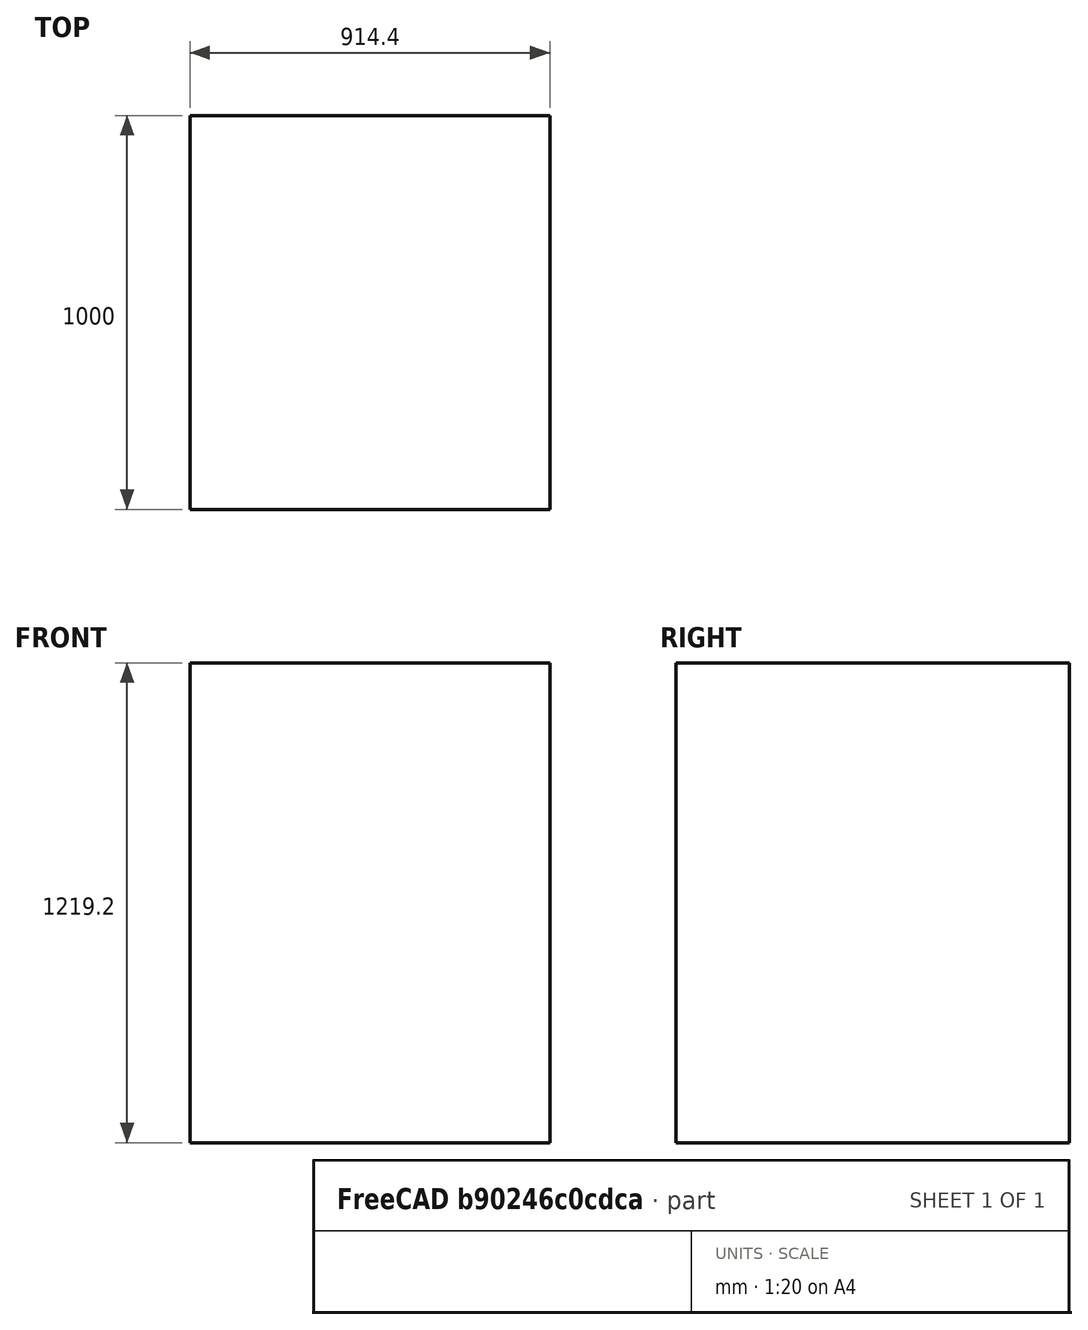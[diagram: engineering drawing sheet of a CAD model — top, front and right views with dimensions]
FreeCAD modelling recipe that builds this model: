
FCSTD DOCUMENT  (FreeCAD 1.0R39319 (Git))
Label: Box-VarSet-Example-v2
License: All rights reserved
LicenseURL: https://en.wikipedia.org/wiki/All_rights_reserved
objects: App::VarSet×1, Part::Box×1
note: 1 computed .brp shape members not serialized (recipe doc carries the construction recipe); baked Part::Feature solids carry a one-line shape summary decoded from their .brp

FEATURE [App::VarSet] VarSet  label="PQs"
  CalcsLiveMappings = {\n  "docVersion": "0.2",\n  "unitsSchema": "UserPreferred",\n  "articleId": "3MAV4GNFQ-3FU",\n  "articleTitle": "calc for freecad demo 1: (LxWxH, rho) => (V, m)",\n  "lastUpdated": "2025-11-08T05:29:35.777Z",\n  "pqMappings": {\n    "Length": {\n      "symbol": "L",\n      "faceUnit": "m"\n    },\n    "Width": {\n      "symbol": "W",\n      "faceUnit": "m"\n    },\n    "Height": {\n      "symbol": "H",\n      "faceUnit": "m"\n    },\n    "Len": {\n      "symbol": "L",\n      "faceUnit": "m"\n    }\n  }\n}
  Height = 1219.2
  Len = 914.4
  Length = 1000
  Width = 1000
FEATURE [Part::Box] Box  label="Cube"
  AttacherType = Attacher::AttachEngine3D
  Height = 1219.2
  Length = 914.4
  Width = 1000
  expr: Height = <<PQs>>.Height
  expr: Length = <<PQs>>.Len
  expr: Width = <<PQs>>.Width
